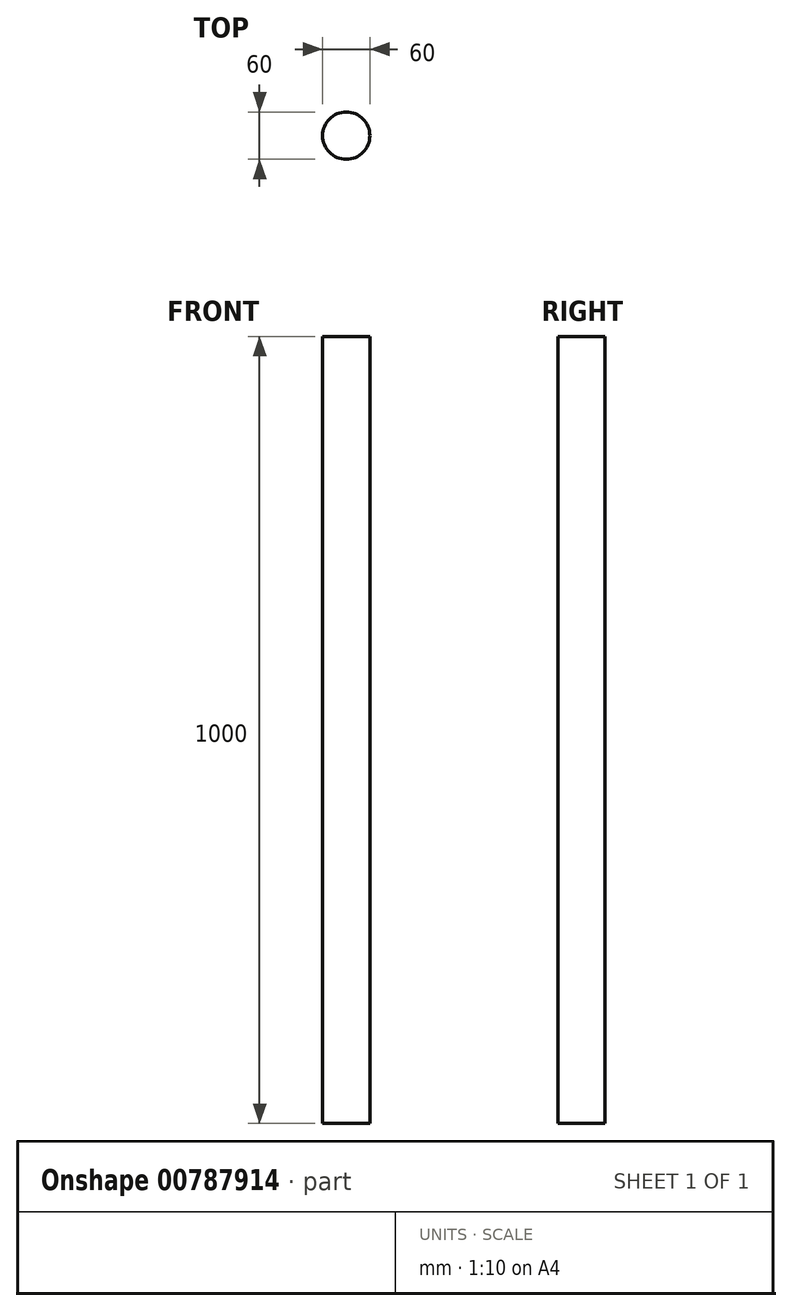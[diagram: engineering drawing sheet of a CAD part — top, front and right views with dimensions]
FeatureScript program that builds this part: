
annotation { "Feature Type Name" : "Feature", "Feature Type Description" : "" }
export const myFeature = defineFeature(function(context is Context, id is Id, definition is map)
    precondition{}
    {
        {
            var Q0;
            Q0=qCreatedBy(makeId("Top.planeOp"),FACE);
            var sketch = newSketch(context, id + "F0", { "sketchPlane" : qUnion([Q0])});
            skCircle(sketch, "E0", {"center": v(0, 0) * mm, "radius": 30 * mm});
            skSolve(sketch);
        }
        {
            var Q0;
            Q0 = qSketchRegion(id + "F0", true);
            extrude(context, id + "F1", {"entities" : qUnion([Q0]), "depth" : 1000 * mm, "offsetDistance" : 25 * mm});
        }
    });
